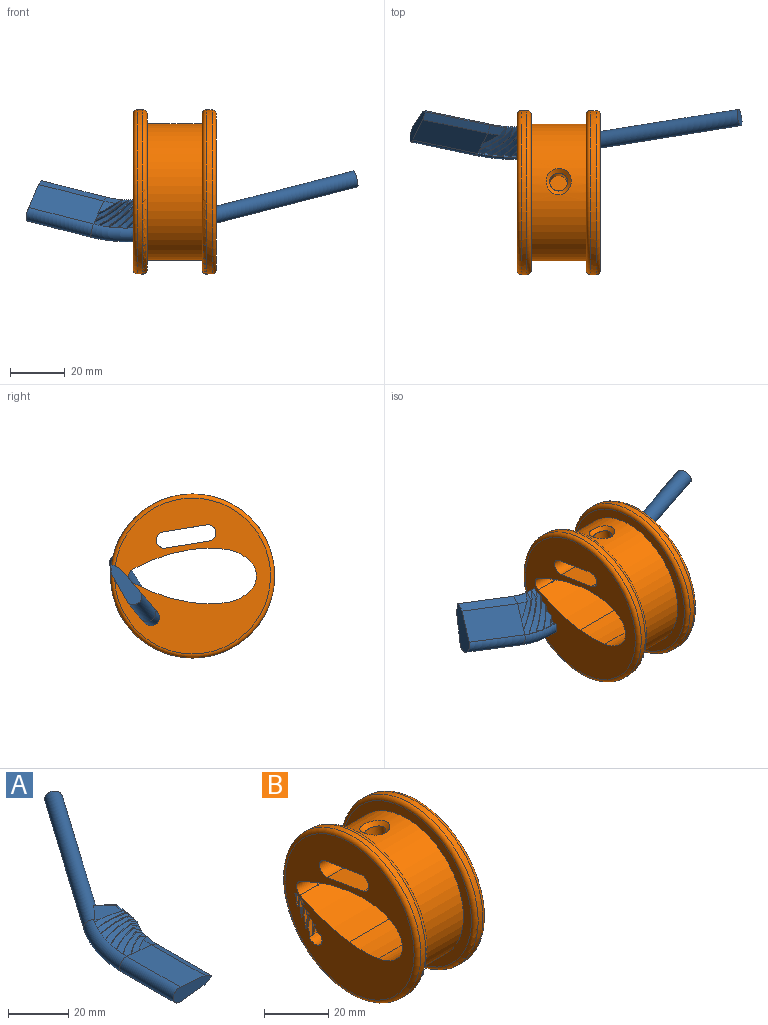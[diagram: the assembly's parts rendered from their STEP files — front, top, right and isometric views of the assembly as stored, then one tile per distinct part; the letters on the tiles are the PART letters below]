
ASSEMBLY  parts=2 mates=1
PART A: 140 faces, bbox 59.3x111.2x8.1 mm
  f0: plane 2.22x1.53mm, normal (0,1,0), area 1.9mm2, adj f4,f25,f127,f128
  f1: plane 4.02x1.91mm, normal (0,1,0), area 2.6mm2, adj f25,f99,f100,f101,f103
  f2: plane 4.02x1.91mm, normal (0,1,0), area 2.6mm2, adj f24,f132,f133,f134,f135
  f3: plane 2.22x1.53mm, normal (0,1,0), area 1.9mm2, adj f11,f24,f116,f117
  f4: cone r=39.7mm half-angle=13.2deg, axis (0,0,-1), area 0.8mm2, adj f0,f18,f127,f129
  f5: cone r=39.7mm half-angle=13.2deg, axis (0,0,-1), area 2.3mm2, adj f18,f105,f106,f107
  f6: cone r=39.7mm half-angle=13.2deg, axis (0,0,-1), area 2.3mm2, adj f18,f112,f113,f114
  f7: cone r=39.7mm half-angle=13.2deg, axis (0,0,-1), area 2.3mm2, adj f18,f108,f110,f111
  f8: cone r=39.7mm half-angle=13.2deg, axis (0,0,-1), area 2.3mm2, adj f18,f123,f124,f125
  f9: cone r=39.7mm half-angle=13.2deg, axis (0,0,-1), area 2.3mm2, adj f18,f119,f120,f121
  f10: cone r=39.7mm half-angle=13.2deg, axis (0,0,-1), area 2.3mm2, adj f18,f136,f137,f139
  f11: cone r=39mm half-angle=13.2deg, axis (0,0,1), area 0.8mm2, adj f3,f18,f116,f118
  f12: cone r=39mm half-angle=13.2deg, axis (0,0,1), area 2.3mm2, adj f18,f95,f96,f97
  f13: cone r=39mm half-angle=13.2deg, axis (0,0,1), area 2.3mm2, adj f18,f87,f88,f89
  f14: cone r=39mm half-angle=13.2deg, axis (0,0,1), area 2.3mm2, adj f18,f91,f92,f93
  f15: cone r=39mm half-angle=13.2deg, axis (0,0,1), area 2.3mm2, adj f18,f76,f77,f78
  f16: cone r=39mm half-angle=13.2deg, axis (0,0,1), area 2.3mm2, adj f18,f80,f81,f82
  f17: cone r=39mm half-angle=13.2deg, axis (0,0,1), area 2.3mm2, adj f18,f83,f84,f85
  f18: torus R=40mm, axis (0,0,1), area 256mm2, adj f4,f5,f6,f7,f8,f9,f10,f11
  f19: cylinder r=3mm len=64.88mm, axis (-0.57,-0.82,0), area 1350.3mm2, adj f18,f20,f63,f64,f66,f69,f72
  f20: plane 6x4.92mm, normal (0.57,0.82,0), area 28.3mm2, adj f19
  f21: cylinder r=3mm len=25mm, axis (0,1,0), area 250.7mm2, adj f18,f22,f24,f25
  f22: plane 18x6mm, normal (0,-1,0), area 78.1mm2, adj f21,f23,f24,f25,f26,f27
  f23: plane 25x0.5mm, normal (1,0,0), area 12.5mm2, adj f22,f26,f27,f60
  f24: plane 25x11.71mm, normal (0.1,0,0.99), area 294.3mm2, adj f2,f3,f21,f22,f27,f30,f38
  f25: plane 25x11.71mm, normal (0.1,0,-0.99), area 294.3mm2, adj f0,f1,f21,f22,f26,f32,f52
  f26: plane 25x2.99mm, normal (0.46,0,-0.89), area 84.1mm2, adj f22,f23,f25,f55
  f27: plane 25x2.99mm, normal (0.46,0,0.89), area 84.1mm2, adj f22,f23,f24,f31
  f28: cone r=25mm half-angle=84.2deg, axis (0,0,-1), area 3.2mm2, adj f18,f29,f127,f129,f130,f137
  f29: cone r=27.98mm half-angle=62.5deg, axis (0,0,-1), area 4.2mm2, adj f28,f60,f127,f130,f137
  f30: cone r=25mm half-angle=84.2deg, axis (0,0,1), area 14.2mm2, adj f24,f31,f133,f134
  f31: cone r=25mm half-angle=62.5deg, axis (0,0,1), area 17.5mm2, adj f27,f30,f60,f133
  f32: cone r=25mm half-angle=84.2deg, axis (0,0,-1), area 3mm2, adj f25,f35,f100,f101,f102,f128
  f33: cone r=25mm half-angle=84.2deg, axis (0,0,-1), area 3.2mm2, adj f18,f36,f119,f121,f122,f124
  f34: cone r=25mm half-angle=84.2deg, axis (0,0,-1), area 3.2mm2, adj f18,f37,f120,f136,f138,f139
  f35: cone r=27.98mm half-angle=62.5deg, axis (0,0,-1), area 4.2mm2, adj f32,f60,f100,f102,f128
  f36: cone r=27.98mm half-angle=62.5deg, axis (0,0,-1), area 4.2mm2, adj f33,f60,f119,f122,f124
  f37: cone r=27.98mm half-angle=62.5deg, axis (0,0,-1), area 4.2mm2, adj f34,f60,f120,f136,f138
  f38: cone r=25mm half-angle=84.2deg, axis (0,0,1), area 3.1mm2, adj f24,f39,f117,f131,f132,f135
  f39: cone r=25mm half-angle=62.5deg, axis (0,0,1), area 4.2mm2, adj f38,f60,f117,f131,f132
  f40: cone r=25mm half-angle=84.2deg, axis (0,0,-1), area 2.1mm2, adj f18,f43,f108,f109,f110,f114
  f41: cone r=25mm half-angle=84.2deg, axis (0,0,-1), area 3.2mm2, adj f18,f67,f111,f123,f125,f126
  f42: cone r=25mm half-angle=84.2deg, axis (0,0,-1), area 0.8mm2, adj f18,f44,f104,f107,f112
  f43: plane 3.61x0.48mm, normal (0.11,-0.02,-0.99), area 1.3mm2, adj f40,f45,f109,f110,f114
  f44: plane 6.79x0.8mm, normal (0.11,-0.02,-0.99), area 2.7mm2, adj f42,f70,f104,f107,f112,f113
  f45: cone r=27.98mm half-angle=62.5deg, axis (0,0,-1), area 1.2mm2, adj f43,f70,f110,f114
  f46: cone r=25mm half-angle=84.2deg, axis (0,0,1), area 3.3mm2, adj f18,f56,f96,f115,f116,f118
  f47: cone r=25mm half-angle=84.2deg, axis (0,0,1), area 0.8mm2, adj f18,f53,f80,f85,f86
  f48: cone r=25mm half-angle=84.2deg, axis (0,0,1), area 3.3mm2, adj f18,f57,f87,f89,f90,f92
  f49: cone r=25mm half-angle=84.2deg, axis (0,0,1), area 3.3mm2, adj f18,f58,f88,f95,f97,f98
  f50: cone r=25mm half-angle=84.2deg, axis (0,0,1), area 2.2mm2, adj f18,f54,f76,f77,f79,f82
  f51: cone r=25mm half-angle=84.2deg, axis (0,0,1), area 3.3mm2, adj f18,f68,f78,f91,f93,f94
  f52: cone r=25mm half-angle=84.2deg, axis (0,0,-1), area 14.2mm2, adj f25,f55,f99,f103
  f53: plane 6.79x0.81mm, normal (0.11,-0.02,0.99), area 2.7mm2, adj f47,f75,f80,f81,f85,f86
  f54: plane 3.61x0.48mm, normal (0.11,-0.02,0.99), area 1.3mm2, adj f50,f59,f77,f79,f82
  f55: cone r=27.98mm half-angle=62.5deg, axis (0,0,-1), area 17.5mm2, adj f26,f52,f60,f103
  f56: cone r=25mm half-angle=62.5deg, axis (0,0,1), area 4.2mm2, adj f46,f60,f96,f115,f116
  f57: cone r=25mm half-angle=62.5deg, axis (0,0,1), area 4.2mm2, adj f48,f60,f87,f90,f92
  f58: cone r=25mm half-angle=62.5deg, axis (0,0,1), area 4.2mm2, adj f49,f60,f88,f95,f98
  f59: cone r=25mm half-angle=62.5deg, axis (0,0,1), area 1.2mm2, adj f54,f75,f77,f82
  f60: cylinder r=25mm len=14.34mm, axis (0,0,1), area 7.4mm2, adj f23,f29,f31,f35,f36,f37,f39,f55
  f61: cone r=25mm half-angle=84.2deg, axis (0,0,1), area 1.6mm2, adj f18,f64,f83
  f62: cone r=25mm half-angle=84.2deg, axis (0,0,-1), area 1.6mm2, adj f18,f66,f105
  f63: plane 5x3.5mm, normal (0.57,0.82,0), area 4.6mm2, adj f19,f69,f72,f73
  f64: plane 12.22x8.17mm, normal (0.11,-0.02,0.99), area 55.2mm2, adj f19,f61,f72,f75,f83,f84
  f65: plane 10.08x1.5mm, normal (0.99,-0.15,0), area 1.5mm2, adj f60,f70,f73,f75
  f66: plane 12.22x8.17mm, normal (0.11,-0.02,-0.99), area 55.2mm2, adj f19,f62,f69,f70,f105,f106
  f67: cone r=27.98mm half-angle=62.5deg, axis (0,0,-1), area 3.5mm2, adj f41,f60,f70,f111,f123,f126
  f68: cone r=25mm half-angle=62.5deg, axis (0,0,1), area 3.5mm2, adj f51,f60,f75,f78,f91,f94
  f69: cylinder r=1.6mm len=6.8mm, axis (-0.82,0.57,-0.1), area 16.5mm2, adj f19,f63,f66,f71
  f70: cylinder r=1.6mm len=10.31mm, axis (-0.15,-0.99,0), area 14.9mm2, adj f44,f45,f60,f65,f66,f67,f71,f106
  f71: sphere r=1.6mm, area 2.6mm2, adj f69,f70,f73
  f72: cylinder r=1.6mm len=6.8mm, axis (-0.82,0.57,0.1), area 16.5mm2, adj f19,f63,f64,f74
  f73: cylinder r=1.6mm len=1.55mm, axis (0,0,1), area 0.3mm2, adj f63,f65,f71,f74
  f74: sphere r=1.6mm, area 2.6mm2, adj f72,f73,f75
  f75: cylinder r=1.6mm len=10.31mm, axis (0.15,0.99,0), area 14.9mm2, adj f53,f59,f60,f64,f65,f68,f74,f77
  f76: bspline ~16.02x2.59mm, area 0.4mm2, adj f15,f50,f77
  f77: bspline ~19.54x5.5mm, area 45.4mm2, adj f15,f50,f54,f59,f75,f76,f78,f79
  f78: bspline ~19.12x3.9mm, area 24.3mm2, adj f15,f51,f68,f75,f77
  f79: bspline ~16.17x2.23mm, area 0mm2, adj f50,f54,f77
  f80: bspline ~16.16x2.19mm, area 0.4mm2, adj f16,f47,f53,f81
  f81: bspline ~19.53x4.7mm, area 41.3mm2, adj f16,f53,f75,f80,f82
  f82: bspline ~16.56x2.8mm, area 23.1mm2, adj f16,f50,f54,f59,f75,f81
  f83: bspline ~16.19x2.19mm, area 0.2mm2, adj f17,f61,f64,f84
  f84: bspline ~19.47x3.86mm, area 36.5mm2, adj f17,f64,f75,f83,f85
  f85: bspline ~15.35x2.71mm, area 20.1mm2, adj f17,f47,f53,f75,f84,f86
  f86: bspline ~16.21x2.25mm, area 0mm2, adj f47,f53,f85
  f87: bspline ~18.24x8.12mm, area 46.1mm2, adj f13,f48,f57,f60,f88,f89,f90
  f88: bspline ~18.22x7.15mm, area 24.6mm2, adj f13,f49,f58,f60,f87
  f89: bspline ~15.37x5.1mm, area 0.4mm2, adj f13,f48,f87
  f90: bspline ~15.69x4.15mm, area 0mm2, adj f48,f57,f87
  f91: bspline ~19.4x6.76mm, area 46.1mm2, adj f14,f51,f60,f68,f92,f93,f94
  f92: bspline ~18.74x5.55mm, area 24.6mm2, adj f14,f48,f57,f60,f91
  f93: bspline ~15.75x3.74mm, area 0.4mm2, adj f14,f51,f91
  f94: bspline ~15.99x2.77mm, area 0mm2, adj f51,f68,f91
  f95: bspline ~17.83x9.55mm, area 46.1mm2, adj f12,f49,f58,f60,f96,f97,f98
  f96: bspline ~17.56x8.7mm, area 24.6mm2, adj f12,f46,f56,f60,f95
  f97: bspline ~14.87x6.42mm, area 0.4mm2, adj f12,f49,f95
  f98: bspline ~15.27x5.51mm, area 0mm2, adj f49,f58,f95
  f99: bspline ~12.82x9.95mm, area 0mm2, adj f1,f52,f103
  f100: bspline ~17.38x12.63mm, area 31.2mm2, adj f1,f32,f35,f60,f101,f102,f103
  f101: bspline ~13.53x8.9mm, area 0.1mm2, adj f1,f32,f100
  f102: bspline ~14.08x8.07mm, area 0mm2, adj f32,f35,f100
  f103: bspline ~15.85x11.59mm, area 14.7mm2, adj f1,f52,f55,f60,f99,f100
  f104: bspline ~16.21x2.25mm, area 0mm2, adj f42,f44,f107
  f105: bspline ~16.19x2.19mm, area 0.2mm2, adj f5,f62,f66,f106
  f106: bspline ~19.47x3.86mm, area 36.5mm2, adj f5,f66,f70,f105,f107
  f107: bspline ~15.35x2.71mm, area 20.1mm2, adj f5,f42,f44,f70,f104,f106
  f108: bspline ~16.02x2.59mm, area 0.4mm2, adj f7,f40,f110
  f109: bspline ~16.17x2.23mm, area 0mm2, adj f40,f43,f110
  f110: bspline ~19.54x5.5mm, area 45.4mm2, adj f7,f40,f43,f45,f70,f108,f109,f111
  f111: bspline ~17.5x3.84mm, area 24.3mm2, adj f7,f41,f67,f70,f110
  f112: bspline ~16.16x2.19mm, area 0.4mm2, adj f6,f42,f44,f113
  f113: bspline ~19.53x4.7mm, area 41.3mm2, adj f6,f44,f70,f112,f114
  f114: bspline ~16.56x2.8mm, area 23.1mm2, adj f6,f40,f43,f45,f70,f113
  f115: bspline ~14.73x6.82mm, area 0mm2, adj f46,f56,f116
  f116: bspline ~16.78x10.52mm, area 44.4mm2, adj f3,f11,f46,f56,f60,f115,f117,f118
  f117: bspline ~16.77x10.18mm, area 21.5mm2, adj f3,f38,f39,f60,f116
  f118: bspline ~14.25x7.69mm, area 0.4mm2, adj f11,f46,f116
  f119: bspline ~19.11x8.33mm, area 46.1mm2, adj f9,f33,f36,f60,f120,f121,f122
  f120: bspline ~17.41x6.98mm, area 24.6mm2, adj f9,f34,f37,f60,f119
  f121: bspline ~15.37x5.1mm, area 0.4mm2, adj f9,f33,f119
  f122: bspline ~15.69x4.15mm, area 0mm2, adj f33,f36,f119
  f123: bspline ~19.4x6.76mm, area 46.1mm2, adj f8,f41,f60,f67,f124,f125,f126
  f124: bspline ~17.91x5.44mm, area 24.6mm2, adj f8,f33,f36,f60,f123
  f125: bspline ~15.75x3.74mm, area 0.4mm2, adj f8,f41,f123
  f126: bspline ~15.99x2.77mm, area 0mm2, adj f41,f67,f123
  f127: bspline ~18.1x11.28mm, area 44.4mm2, adj f0,f4,f28,f29,f60,f128,f129,f130
  f128: bspline ~14.14x8.34mm, area 21.5mm2, adj f0,f32,f35,f60,f127
  f129: bspline ~14.25x7.69mm, area 0.4mm2, adj f4,f28,f127
  f130: bspline ~14.73x6.82mm, area 0mm2, adj f28,f29,f127
  f131: bspline ~14.08x8.07mm, area 0mm2, adj f38,f39,f132
  f132: bspline ~17.38x12.63mm, area 31.2mm2, adj f2,f38,f39,f60,f131,f133,f135
  f133: bspline ~15.85x11.59mm, area 14.7mm2, adj f2,f30,f31,f60,f132,f134
  f134: bspline ~12.82x9.95mm, area 0mm2, adj f2,f30,f133
  f135: bspline ~13.53x8.9mm, area 0.1mm2, adj f2,f38,f132
  f136: bspline ~18.68x9.84mm, area 46.1mm2, adj f10,f34,f37,f60,f137,f138,f139
  f137: bspline ~16.77x8.45mm, area 24.6mm2, adj f10,f28,f29,f60,f136
  f138: bspline ~15.27x5.51mm, area 0mm2, adj f34,f37,f136
  f139: bspline ~14.87x6.42mm, area 0.4mm2, adj f10,f34,f136
PART B: 113 faces, bbox 42.7x65.4x65.4 mm
  f0: plane 57.45x57.45mm, normal (1,0,0), area 1684.4mm2, adj f7,f11,f12,f13,f14,f15,f16,f17
  f1: cylinder r=30mm len=60mm, axis (-1,0,0), area 395.8mm2, adj f7,f8
  f2: plane 57x57mm, normal (-1,0,0), area 588.3mm2, adj f3,f8
  f3: cylinder r=25mm len=50mm, axis (-1,0,0), area 3101.8mm2, adj f2,f4,f24,f26,f27,f28,f29
  f4: plane 57x57mm, normal (1,0,0), area 588.3mm2, adj f3,f9
  f5: cylinder r=30mm len=60mm, axis (-1,0,0), area 395.8mm2, adj f9,f10
  f6: plane 57.09x57.09mm, normal (-1,0,0), area 1652.6mm2, adj f10,f11,f12,f13,f14,f15,f16,f17
  f7: torus R=28.5mm, axis (-1,0,0), area 436.1mm2, adj f0,f1
  f8: torus R=28.5mm, axis (1,0,0), area 436.1mm2, adj f1,f2
  f9: torus R=28.5mm, axis (1,0,0), area 436.1mm2, adj f4,f5
  f10: torus R=28.5mm, axis (-1,0,0), area 436.1mm2, adj f5,f6
  f11: cylinder r=64mm len=30.4mm, axis (1,0,0), area 697.9mm2, adj f0,f6,f12,f18
  f12: cylinder r=44mm len=30.4mm, axis (1,0,0), area 391.5mm2, adj f0,f6,f11,f13
  f13: cylinder r=15mm len=30.4mm, axis (1,0,0), area 301.9mm2, adj f0,f6,f12,f14
  f14: cylinder r=7.5mm len=30.4mm, axis (1,0,0), area 345.3mm2, adj f0,f6,f13,f15
  f15: cylinder r=15mm len=30.4mm, axis (1,0,0), area 301.9mm2, adj f0,f6,f14,f16
  f16: cylinder r=44mm len=30.4mm, axis (1,0,0), area 391.5mm2, adj f0,f6,f15,f17
  f17: cylinder r=64mm len=30.4mm, axis (1,0,0), area 697.9mm2, adj f0,f6,f16,f18
  f18: cylinder r=2.9mm len=30.4mm, axis (1,0,0), area 188.8mm2, adj f0,f6,f11,f17
  f19: plane 30.4x15.79mm, normal (0,-0.16,-0.99), area 452.2mm2, adj f0,f6,f20,f22,f23
  f20: cylinder r=3mm len=30.4mm, axis (1,0,0), area 286.5mm2, adj f0,f6,f19,f21
  f21: plane 30.4x15.79mm, normal (0,0.16,0.99), area 486.4mm2, adj f0,f6,f20,f22
  f22: cylinder r=3mm len=30.4mm, axis (1,0,0), area 286.5mm2, adj f0,f6,f19,f21
  f23: cylinder r=3.3mm len=7.42mm, axis (0,0.16,0.99), area 116mm2, adj f19,f24
  f24: bspline ~9.6x9.22mm, area 49.3mm2, adj f3,f23
  f25: cylinder r=3mm len=23.43mm, axis (-0.96,-0.15,-0.25), area 346.7mm2, adj f0,f36,f60,f61,f63,f66,f69
  f26: plane 2.99x1.63mm, normal (-0.04,-0.87,0.49), area 1.3mm2, adj f3,f27,f29,f51,f73,f75
  f27: cone r=25mm half-angle=62.5deg, axis (0.02,0.81,-0.58), area 0.9mm2, adj f3,f26,f28,f73
  f28: cylinder r=1.6mm len=10.27mm, axis (0.99,-0.12,-0.13), area 14.8mm2, adj f3,f27,f29,f53,f57,f61,f62,f65
  f29: bspline ~16.3x9.95mm, area 23.1mm2, adj f3,f26,f28,f34,f51,f77
  f30: cone r=39.7mm half-angle=13.2deg, axis (-0.02,-0.81,0.58), area 2.3mm2, adj f36,f93,f94,f95
  f31: cone r=39.7mm half-angle=13.2deg, axis (-0.02,-0.81,0.58), area 2.3mm2, adj f36,f100,f101,f102
  f32: cone r=39.7mm half-angle=13.2deg, axis (-0.02,-0.81,0.58), area 0.3mm2, adj f6,f36,f96,f98
  f33: cone r=39mm half-angle=13.2deg, axis (0.02,0.81,-0.58), area 0.4mm2, adj f6,f36,f72,f73
  f34: cone r=39mm half-angle=13.2deg, axis (0.02,0.81,-0.58), area 2.3mm2, adj f29,f36,f76,f77
  f35: cone r=39mm half-angle=13.2deg, axis (0.02,0.81,-0.58), area 2.3mm2, adj f36,f78,f79,f80
  f36: torus R=40mm, axis (0.02,0.81,-0.58), area 102.9mm2, adj f6,f25,f30,f31,f32,f33,f34,f35
  f37: cone r=27.98mm half-angle=62.5deg, axis (-0.02,-0.81,0.58), area 0.1mm2, adj f6,f57,f111
  f38: cone r=25mm half-angle=84.2deg, axis (-0.02,-0.81,0.58), area 2.1mm2, adj f6,f40,f103,f105,f107
  f39: cone r=25mm half-angle=84.2deg, axis (-0.02,-0.81,0.58), area 0.4mm2, adj f6,f41,f104,f112
  f40: cone r=27.98mm half-angle=62.5deg, axis (-0.02,-0.81,0.58), area 4.2mm2, adj f38,f57,f103,f105,f107
  f41: cone r=27.98mm half-angle=62.5deg, axis (-0.02,-0.81,0.58), area 4.2mm2, adj f39,f57,f104,f110,f112
  f42: cone r=25mm half-angle=84.2deg, axis (-0.02,-0.81,0.58), area 2.2mm2, adj f36,f45,f96,f97,f98,f102
  f43: cone r=25mm half-angle=84.2deg, axis (-0.02,-0.81,0.58), area 3mm2, adj f6,f64,f99,f106,f108,f109
  f44: cone r=25mm half-angle=84.2deg, axis (-0.02,-0.81,0.58), area 0.8mm2, adj f36,f46,f92,f95,f100
  f45: plane 2.56x2.31mm, normal (0,0.74,-0.67), area 1.3mm2, adj f42,f47,f97,f98,f102
  f46: plane 4.92x4.44mm, normal (0,0.74,-0.67), area 2.7mm2, adj f44,f67,f92,f95,f100,f101
  f47: cone r=27.98mm half-angle=62.5deg, axis (-0.02,-0.81,0.58), area 1.2mm2, adj f45,f67,f98,f102
  f48: cone r=25mm half-angle=84.2deg, axis (0.02,0.81,-0.58), area 0.8mm2, adj f36,f53,f76,f80,f81
  f49: cone r=25mm half-angle=84.2deg, axis (0.02,0.81,-0.58), area 2.2mm2, adj f6,f55,f82,f84,f86
  f50: cone r=25mm half-angle=84.2deg, axis (0.02,0.81,-0.58), area 0.4mm2, adj f6,f56,f83,f91
  f51: cone r=25mm half-angle=84.2deg, axis (0.02,0.81,-0.58), area 2.1mm2, adj f26,f29,f36,f72,f73,f75
  f52: cone r=25mm half-angle=84.2deg, axis (0.02,0.81,-0.58), area 3mm2, adj f6,f65,f74,f85,f87,f88
  f53: plane 5.8x3.22mm, normal (-0.04,-0.87,0.49), area 2.7mm2, adj f28,f48,f76,f77,f80,f81
  f54: cone r=25mm half-angle=62.5deg, axis (0.02,0.81,-0.58), area 0.1mm2, adj f6,f57,f90
  f55: cone r=25mm half-angle=62.5deg, axis (0.02,0.81,-0.58), area 4.2mm2, adj f49,f57,f82,f84,f86
  f56: cone r=25mm half-angle=62.5deg, axis (0.02,0.81,-0.58), area 4.2mm2, adj f50,f57,f83,f89,f91
  f57: cylinder r=25mm len=5.25mm, axis (0.02,0.81,-0.58), area 2.5mm2, adj f6,f28,f37,f40,f41,f54,f55,f56
  f58: cone r=25mm half-angle=84.2deg, axis (0.02,0.81,-0.58), area 1.6mm2, adj f36,f61,f78
  f59: cone r=25mm half-angle=84.2deg, axis (-0.02,-0.81,0.58), area 1.6mm2, adj f36,f63,f93
  f60: plane 5.16x4.05mm, normal (-0.96,-0.15,-0.25), area 4.6mm2, adj f25,f66,f69,f70
  f61: plane 10.3x8.35mm, normal (-0.04,-0.87,0.49), area 55.2mm2, adj f25,f28,f58,f69,f78,f79
  f62: plane 10.04x1.37mm, normal (-0.17,-0.57,-0.8), area 1.5mm2, adj f28,f57,f67,f70
  f63: plane 8.76x8.36mm, normal (0,0.74,-0.67), area 55.2mm2, adj f25,f59,f66,f67,f93,f94
  f64: cone r=27.98mm half-angle=62.5deg, axis (-0.02,-0.81,0.58), area 3.5mm2, adj f43,f57,f67,f99,f106,f109
  f65: cone r=25mm half-angle=62.5deg, axis (0.02,0.81,-0.58), area 3.5mm2, adj f28,f52,f57,f74,f85,f88
  f66: cylinder r=1.6mm len=6.2mm, axis (0.29,-0.64,-0.71), area 16.5mm2, adj f25,f60,f63,f68
  f67: cylinder r=1.6mm len=10.34mm, axis (-0.99,0.12,0.13), area 14.9mm2, adj f46,f47,f57,f62,f63,f64,f68,f94
  f68: sphere r=1.6mm, area 2.6mm2, adj f66,f67,f70
  f69: cylinder r=1.6mm len=7.33mm, axis (0.29,-0.48,-0.83), area 16.5mm2, adj f25,f60,f61,f71
  f70: cylinder r=1.6mm len=1.26mm, axis (0.02,0.81,-0.58), area 0.3mm2, adj f60,f62,f68,f71
  f71: sphere r=1.6mm, area 2.6mm2, adj f28,f69,f70
  f72: bspline ~13.12x8.13mm, area 0.4mm2, adj f33,f51,f73
  f73: bspline ~16.7x10.77mm, area 41.6mm2, adj f6,f26,f27,f28,f33,f51,f72,f74
  f74: bspline ~11.87x7.37mm, area 19.5mm2, adj f6,f28,f52,f65,f73
  f75: bspline ~13.5x8.38mm, area 0mm2, adj f26,f51,f73
  f76: bspline ~13.57x8.49mm, area 0.4mm2, adj f34,f48,f53,f77
  f77: bspline ~17.11x9.65mm, area 41.3mm2, adj f28,f29,f34,f53,f76
  f78: bspline ~13.93x8.78mm, area 0.2mm2, adj f35,f58,f61,f79
  f79: bspline ~17.4x10.11mm, area 36.5mm2, adj f28,f35,f61,f78,f80
  f80: bspline ~16.77x10.35mm, area 20.1mm2, adj f28,f35,f48,f53,f79,f81
  f81: bspline ~13.68x8.55mm, area 0mm2, adj f48,f53,f80
  f82: bspline ~13.49x11.01mm, area 13.2mm2, adj f6,f49,f55,f57,f83,f84
  f83: bspline ~12.25x10.01mm, area 5.2mm2, adj f6,f50,f56,f57,f82
  f84: bspline ~12.45x8.84mm, area 0mm2, adj f49,f55,f82
  f85: bspline ~16.18x12.15mm, area 27.1mm2, adj f6,f52,f57,f65,f86,f87,f88
  f86: bspline ~15.02x11.09mm, area 12.5mm2, adj f6,f49,f55,f57,f85
  f87: bspline ~12.58x8.47mm, area 0.1mm2, adj f6,f52,f85
  f88: bspline ~13.02x8mm, area 0mm2, adj f52,f65,f85
  f89: bspline ~12.91x12.01mm, area 2mm2, adj f6,f56,f57,f90,f91
  f90: bspline ~11.54x11.08mm, area 0.2mm2, adj f6,f54,f57,f89
  f91: bspline ~11.8x9.99mm, area 0mm2, adj f6,f50,f56,f89
  f92: bspline ~12.23x10.58mm, area 0mm2, adj f44,f46,f95
  f93: bspline ~12.51x10.76mm, area 0.2mm2, adj f30,f59,f63,f94
  f94: bspline ~14.49x13.59mm, area 36.5mm2, adj f30,f63,f67,f93,f95
  f95: bspline ~11.65x10.5mm, area 20.1mm2, adj f30,f44,f46,f67,f92,f94
  f96: bspline ~11.7x10.11mm, area 0.4mm2, adj f32,f42,f98
  f97: bspline ~12.03x10.42mm, area 0mm2, adj f42,f45,f98
  f98: bspline ~13.56x13.01mm, area 41.4mm2, adj f6,f32,f42,f45,f47,f67,f96,f97
  f99: bspline ~13.66x12.23mm, area 19.3mm2, adj f6,f43,f64,f67,f98
  f100: bspline ~12.15x10.47mm, area 0.4mm2, adj f31,f44,f46,f101
  f101: bspline ~14.07x13.34mm, area 41.3mm2, adj f31,f46,f67,f100,f102
  f102: bspline ~14.27x12.69mm, area 23.1mm2, adj f31,f42,f45,f47,f67,f101
  f103: bspline ~11x10.6mm, area 13mm2, adj f6,f38,f40,f57,f104,f105
  f104: bspline ~10.51x10.01mm, area 5.1mm2, adj f6,f39,f41,f57,f103
  f105: bspline ~10.98x9.6mm, area 0mm2, adj f38,f40,f103
  f106: bspline ~12.95x12.59mm, area 26.8mm2, adj f6,f43,f57,f64,f107,f108,f109
  f107: bspline ~12.94x11.7mm, area 12.3mm2, adj f6,f38,f40,f57,f106
  f108: bspline ~11.16x9.69mm, area 0.1mm2, adj f6,f43,f106
  f109: bspline ~11.55x10.04mm, area 0mm2, adj f43,f64,f106
  f110: bspline ~12.01x10.16mm, area 1.8mm2, adj f6,f41,f57,f111,f112
  f111: bspline ~11.08x9.78mm, area 0.2mm2, adj f6,f37,f57,f110
  f112: bspline ~10.33x10.04mm, area 0mm2, adj f6,f39,f41,f110
PLACE A rot(axis=(-0.78,-0.56,-0.3),137.3deg) t=(-23.05,70.49,5.29)mm
PLACE B t=(-5.86,31.98,-12.04)mm fixed
MATE cylindrical A.f19 <-> B.f25  axis (0.96,0.15,0.25) through (-11.49,47.94,-25.67)mm
